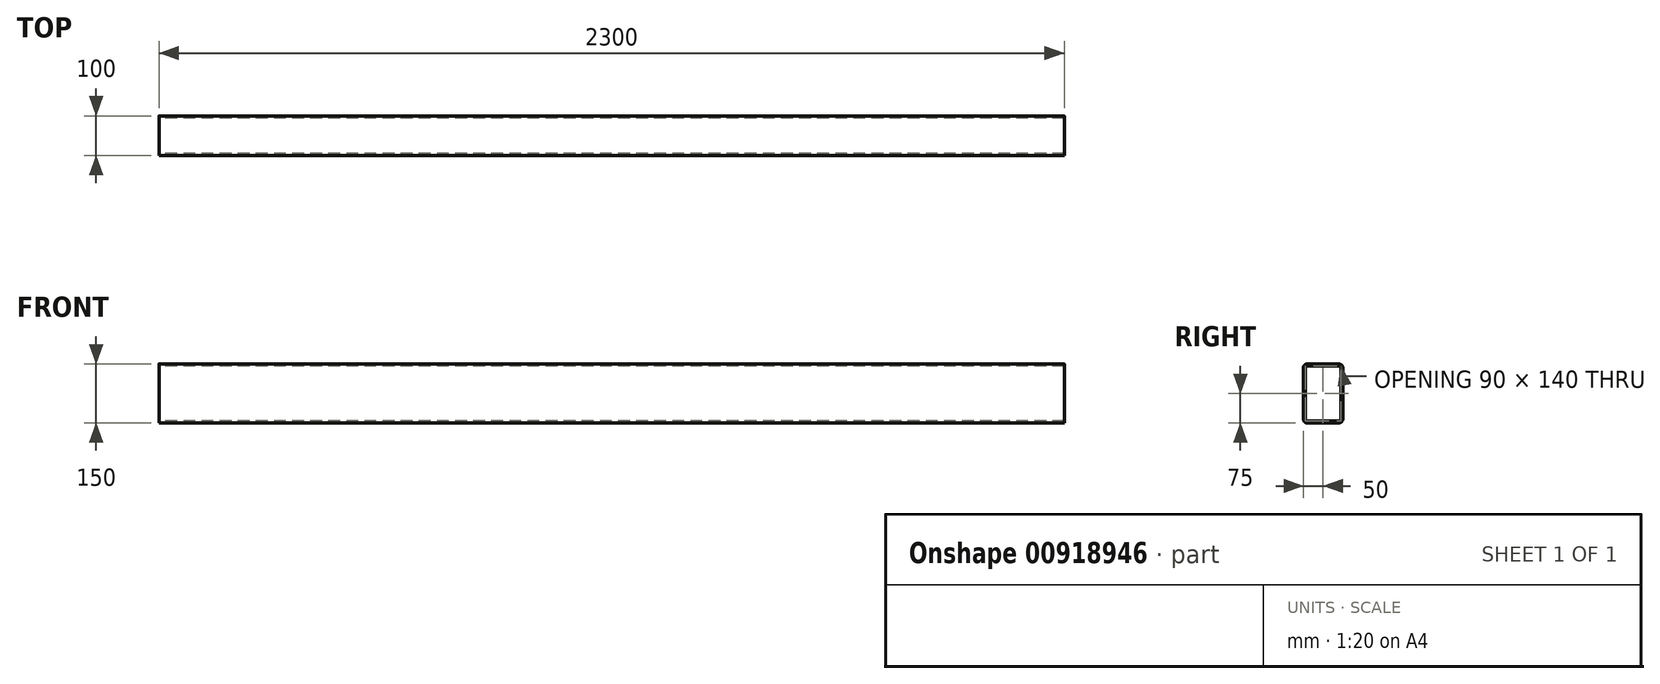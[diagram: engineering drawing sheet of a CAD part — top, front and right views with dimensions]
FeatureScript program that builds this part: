
annotation { "Feature Type Name" : "Feature", "Feature Type Description" : "" }
export const myFeature = defineFeature(function(context is Context, id is Id, definition is map)
    precondition{}
    {
        {
            var Q0;
            Q0=qCreatedBy(makeId("Right.planeOp"),FACE);
            var sketch = newSketch(context, id + "F0", { "sketchPlane" : qUnion([Q0])});
            skLineSegment(sketch, "E0.bottom", {"start": v(40, 75) * mm, "end": v(-40, 75) * mm});
            skLineSegment(sketch, "E0.top", {"start": v(40, -75) * mm, "end": v(-40, -75) * mm});
            skLineSegment(sketch, "E0.left", {"start": v(50, 65) * mm, "end": v(50, -65) * mm});
            skLineSegment(sketch, "E0.right", {"start": v(-50, 65) * mm, "end": v(-50, -65) * mm});
            skPoint(sketch, "E0.middle", {"position": v(0, 0) * mm});
            skPoint(sketch, "E1.visualSharp", {"position": v(-50, 75) * mm});
            skArc(sketch, "E1.filletArc", {"start": v(-40, 75) * mm, "mid": v(-47.07, 72.07) * mm, "end": v(-50, 65) * mm});
            skPoint(sketch, "E2.visualSharp", {"position": v(50, 75) * mm});
            skArc(sketch, "E2.filletArc", {"start": v(50, 65) * mm, "mid": v(47.07, 72.07) * mm, "end": v(40, 75) * mm});
            skPoint(sketch, "E3.visualSharp", {"position": v(50, -75) * mm});
            skArc(sketch, "E3.filletArc", {"start": v(40, -75) * mm, "mid": v(47.07, -72.07) * mm, "end": v(50, -65) * mm});
            skPoint(sketch, "E4.visualSharp", {"position": v(-50, -75) * mm});
            skArc(sketch, "E4.filletArc", {"start": v(-50, -65) * mm, "mid": v(-47.07, -72.07) * mm, "end": v(-40, -75) * mm});
            skLineSegment(sketch, "E5.0", {"start": v(40, -70) * mm, "end": v(-40, -70) * mm});
            skArc(sketch, "E5.1", {"start": v(-45, -65) * mm, "mid": v(-43.54, -68.54) * mm, "end": v(-40, -70) * mm});
            skArc(sketch, "E5.2", {"start": v(40, -70) * mm, "mid": v(43.54, -68.54) * mm, "end": v(45, -65) * mm});
            skLineSegment(sketch, "E5.3", {"start": v(-45, 65) * mm, "end": v(-45, -65) * mm});
            skLineSegment(sketch, "E5.4", {"start": v(45, 65) * mm, "end": v(45, -65) * mm});
            skArc(sketch, "E5.5", {"start": v(45, 65) * mm, "mid": v(43.54, 68.54) * mm, "end": v(40, 70) * mm});
            skLineSegment(sketch, "E5.6", {"start": v(40, 70) * mm, "end": v(-40, 70) * mm});
            skArc(sketch, "E5.7", {"start": v(-40, 70) * mm, "mid": v(-43.54, 68.54) * mm, "end": v(-45, 65) * mm});
            skSolve(sketch);
        }
        {
            var Q0;
            Q0=makeQuery(id+"F0.imprint","IMPRINT",FACE,{"disambiguationData":[TD([[makeQuery(id+"F0.imprint","IMPRINT",EDGE,{"derivedFrom":sQuery(id+"F0.wireOp",EDGE,"E0.bottom")}),1.0]])]});
            extrude(context, id + "F1", {"entities" : qUnion([Q0]), "depth" : 2300 * mm, "offsetDistance" : 25 * mm});
        }
    });
